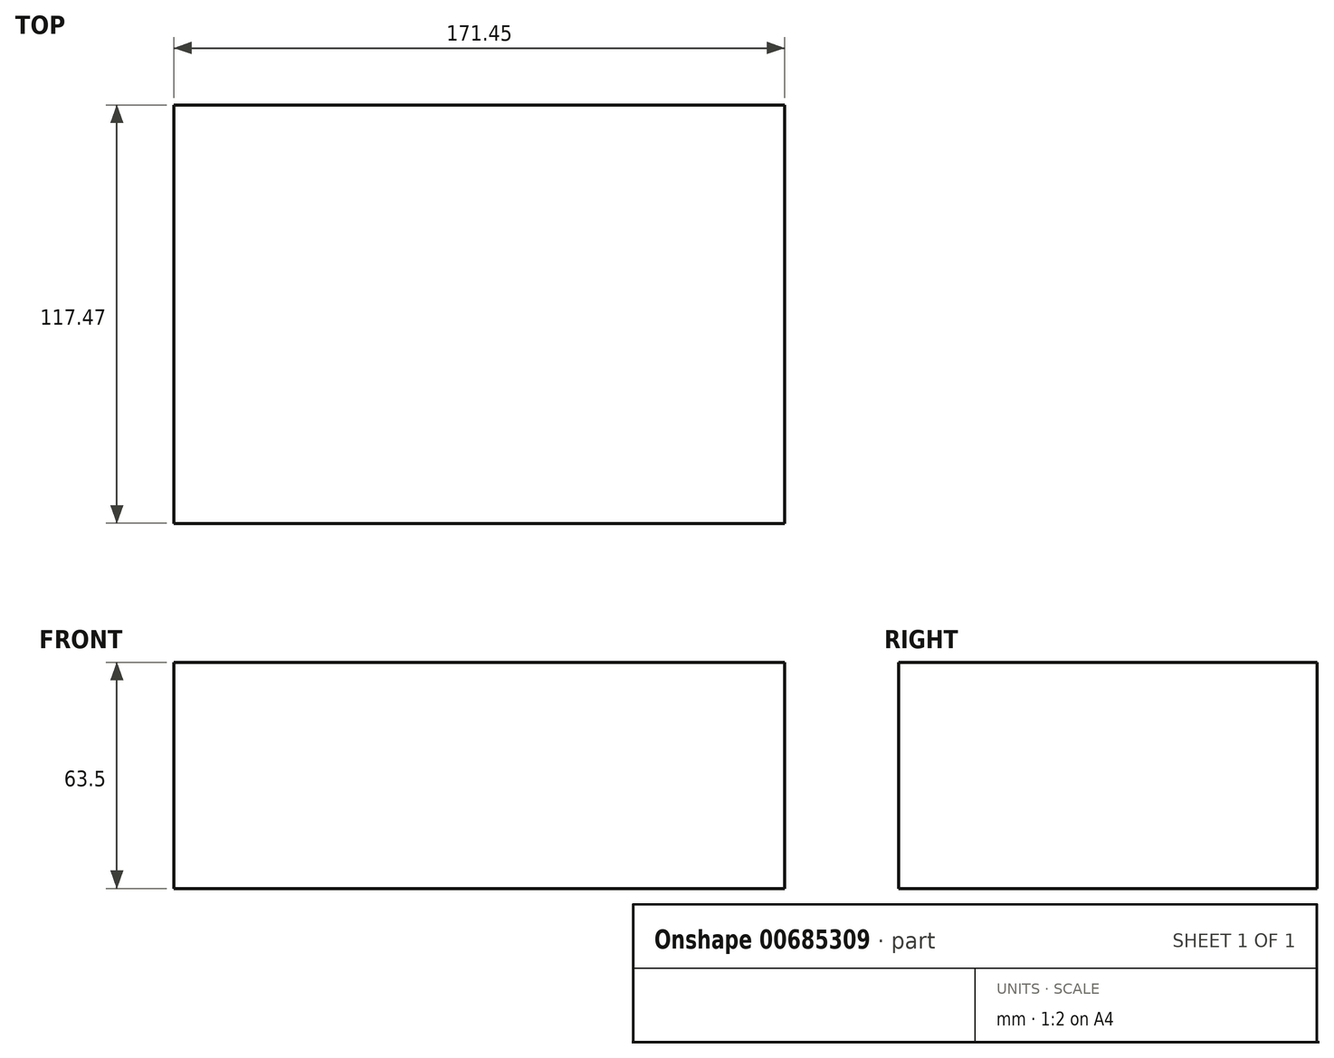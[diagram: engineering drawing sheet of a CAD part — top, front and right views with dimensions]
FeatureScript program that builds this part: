
annotation { "Feature Type Name" : "Feature", "Feature Type Description" : "" }
export const myFeature = defineFeature(function(context is Context, id is Id, definition is map)
    precondition{}
    {
        {
            var Q0;
            Q0=qCreatedBy(makeId("Front.planeOp"),FACE);
            var sketch = newSketch(context, id + "F0", { "sketchPlane" : qUnion([Q0])});
            skLineSegment(sketch, "E0.bottom", {"start": v(0, 0) * mm, "end": v(171.45, 0) * mm});
            skLineSegment(sketch, "E0.top", {"start": v(0, 63.5) * mm, "end": v(171.45, 63.5) * mm});
            skLineSegment(sketch, "E0.left", {"start": v(0, 0) * mm, "end": v(0, 63.5) * mm});
            skLineSegment(sketch, "E0.right", {"start": v(171.45, 0) * mm, "end": v(171.45, 63.5) * mm});
            skSolve(sketch);
        }
        {
            var Q0;
            Q0 = qSketchRegion(id + "F0", true);
            extrude(context, id + "F1", {"entities" : qUnion([Q0]), "depth" : 117.47 * mm, "offsetDistance" : 25.4 * mm});
        }
    });
